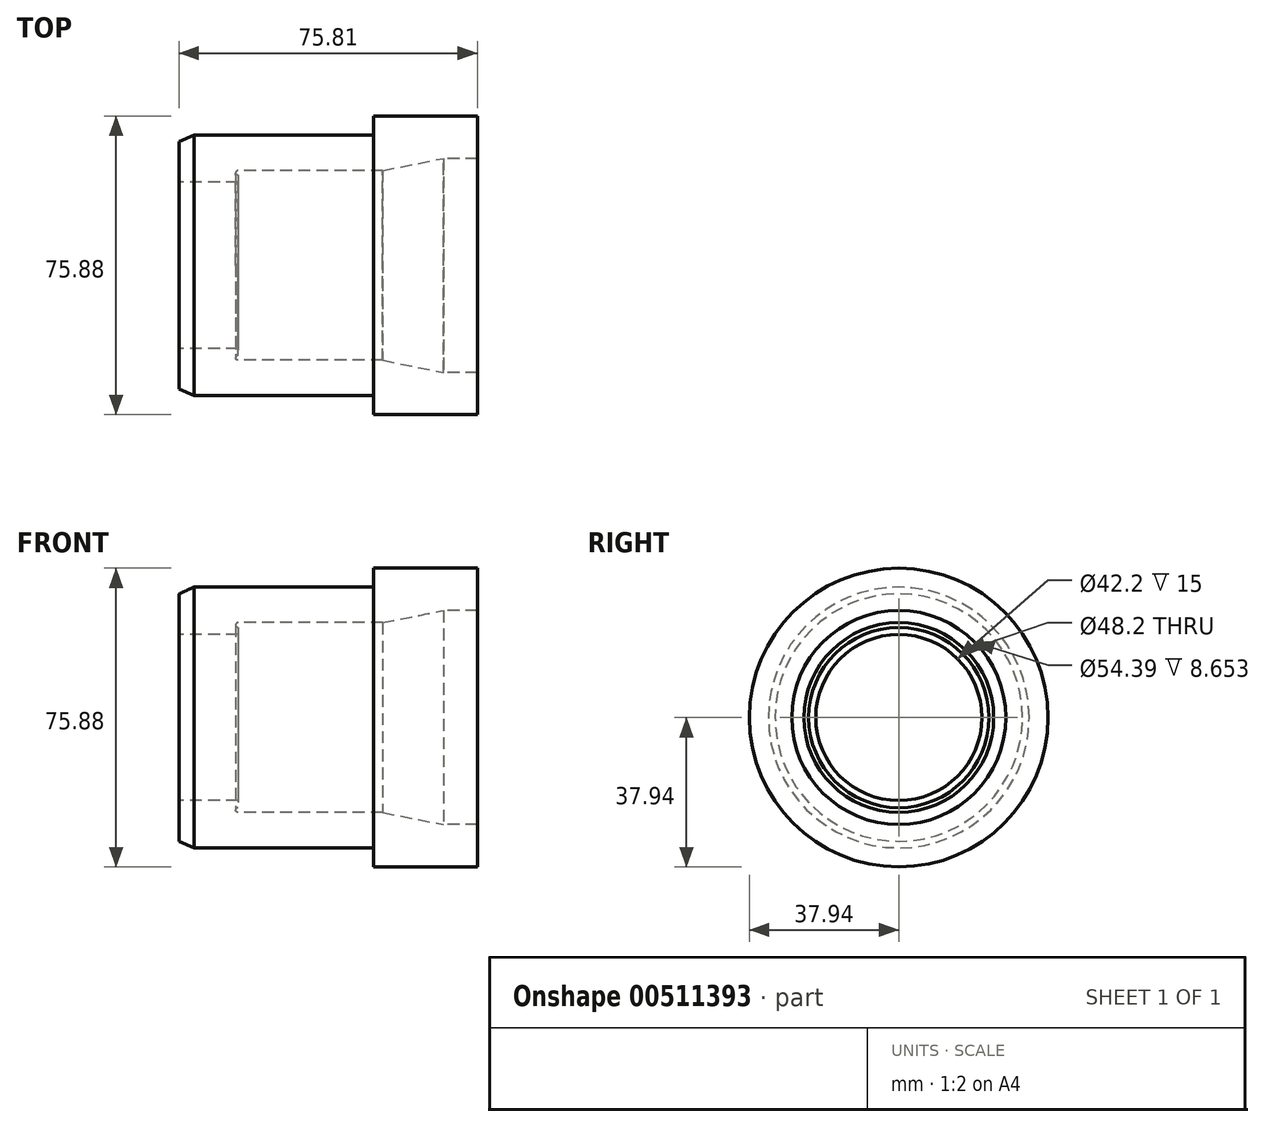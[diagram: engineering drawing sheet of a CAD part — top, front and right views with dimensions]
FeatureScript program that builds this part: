
annotation { "Feature Type Name" : "Feature", "Feature Type Description" : "" }
export const myFeature = defineFeature(function(context is Context, id is Id, definition is map)
    precondition{}
    {
        {
            var Q0;
            Q0=qCreatedBy(makeId("Top.planeOp"),FACE);
            var sketch = newSketch(context, id + "F0", { "sketchPlane" : qUnion([Q0])});
            skLineSegment(sketch, "E0", {"start": v(0, 0) * mm, "end": v(15, 0) * mm});
            skLineSegment(sketch, "E1", {"start": v(15, 0) * mm, "end": v(15, 1.8) * mm});
            skLineSegment(sketch, "E2", {"start": v(15, 1.8) * mm, "end": v(15, 1.8) * mm});
            skLineSegment(sketch, "E3", {"start": v(14.4, 2.4) * mm, "end": v(14.4, 2.4) * mm});
            skLineSegment(sketch, "E4", {"start": v(15, 3) * mm, "end": v(51.74, 3) * mm});
            skLineSegment(sketch, "E5", {"start": v(51.74, 3) * mm, "end": v(67.16, 6.1) * mm});
            skLineSegment(sketch, "E6", {"start": v(67.16, 6.1) * mm, "end": v(75.81, 6.1) * mm});
            skLineSegment(sketch, "E7", {"start": v(75.81, 6.1) * mm, "end": v(75.81, 16.84) * mm});
            skLineSegment(sketch, "E8", {"start": v(0, 0) * mm, "end": v(0, 10.33) * mm});
            skLineSegment(sketch, "E9", {"start": v(0, 10.33) * mm, "end": v(3.79, 12.02) * mm});
            skLineSegment(sketch, "E10", {"start": v(3.79, 12.02) * mm, "end": v(49.37, 12.02) * mm});
            skLineSegment(sketch, "E11", {"start": v(49.37, 16.84) * mm, "end": v(49.37, 12.02) * mm});
            skLineSegment(sketch, "E12", {"start": v(49.37, 16.84) * mm, "end": v(75.81, 16.84) * mm});
            skPoint(sketch, "E13.visualSharp", {"position": v(14.4, 1.8) * mm});
            skArc(sketch, "E13.filletArc", {"start": v(14.4, 2.4) * mm, "mid": v(14.58, 1.98) * mm, "end": v(15, 1.8) * mm});
            skPoint(sketch, "E14.visualSharp", {"position": v(14.4, 3) * mm});
            skArc(sketch, "E14.filletArc", {"start": v(15, 3) * mm, "mid": v(14.58, 2.82) * mm, "end": v(14.4, 2.4) * mm});
            skLineSegment(sketch, "E15", {"start": v(-34.41, -21.1) * mm, "end": v(87.43, -21.1) * mm});
            skSolve(sketch);
        }
        {
            var Q0;
            Q0 = qSketchRegion(id + "F0", true);
            var Q1;
            Q1=sQuery(id+"F0.wireOp",EDGE,"E15");
            revolve(context, id + "F1", {"entities" : qUnion([Q0]), "axis" : qUnion([Q1]), "revolveType" : RevolveType.FULL});
        }
    });
